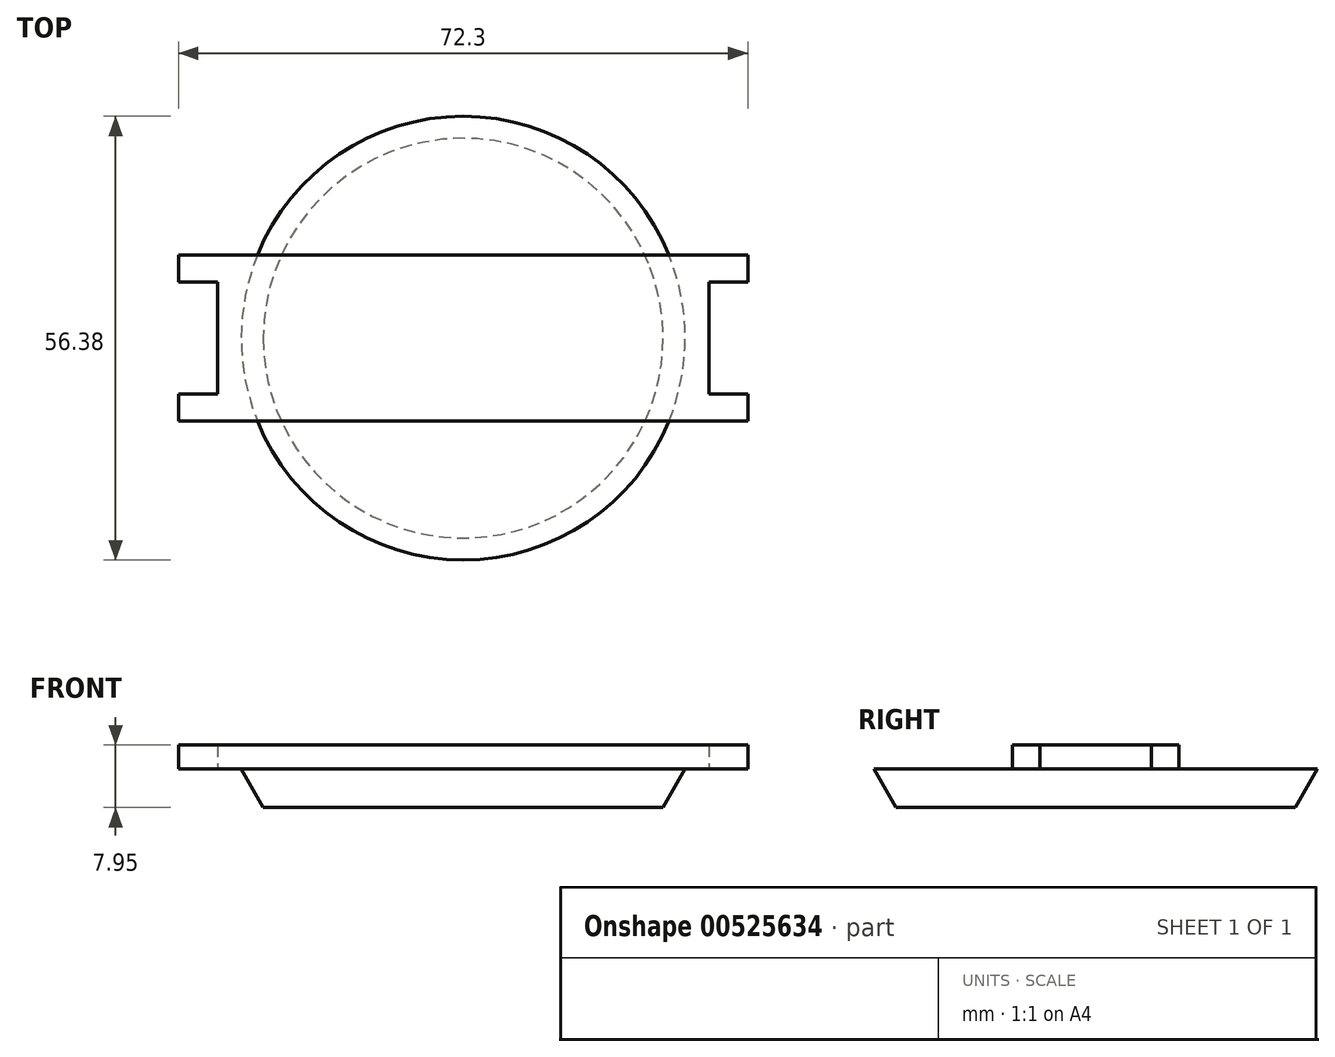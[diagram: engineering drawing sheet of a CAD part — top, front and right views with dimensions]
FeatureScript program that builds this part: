
annotation { "Feature Type Name" : "Feature", "Feature Type Description" : "" }
export const myFeature = defineFeature(function(context is Context, id is Id, definition is map)
    precondition{}
    {
        {
            var Q0;
            Q0=qCreatedBy(makeId("Front.planeOp"),FACE);
            var sketch = newSketch(context, id + "F0", { "sketchPlane" : qUnion([Q0])});
            skLineSegment(sketch, "E0", {"start": v(0, 0) * mm, "end": v(28.19, 0) * mm});
            skLineSegment(sketch, "E1", {"start": v(28.19, 0) * mm, "end": v(25.39, -4.95) * mm});
            skLineSegment(sketch, "E2", {"start": v(25.39, -4.95) * mm, "end": v(0, -4.95) * mm});
            skLineSegment(sketch, "E3", {"start": v(0, -4.95) * mm, "end": v(0, 0) * mm});
            skSolve(sketch);
        }
        {
            var Q0;
            Q0=makeQuery(id+"F0.imprint","IMPRINT",FACE,{"disambiguationData":[TD([[makeQuery(id+"F0.imprint","IMPRINT",EDGE,{"derivedFrom":sQuery(id+"F0.wireOp",EDGE,"E0")}),-1.0]])]});
            var Q1;
            Q1=sQuery(id+"F0.wireOp",EDGE,"E3");
            revolve(context, id + "F1", {"entities" : qUnion([Q0]), "axis" : qUnion([Q1]), "revolveType" : RevolveType.FULL});
        }
        {
            var Q0;
            Q0=qCreatedBy(makeId("Top.planeOp"),FACE);
            var sketch = newSketch(context, id + "F2", { "sketchPlane" : qUnion([Q0])});
            skLineSegment(sketch, "E4", {"start": v(-36.15, -10.54) * mm, "end": v(0, -10.54) * mm});
            skLineSegment(sketch, "E5", {"start": v(-36.15, -10.54) * mm, "end": v(-36.15, -7.1) * mm});
            skLineSegment(sketch, "E6", {"start": v(-36.15, -7.1) * mm, "end": v(-31.2, -7.1) * mm});
            skLineSegment(sketch, "E7", {"start": v(-31.2, -7.1) * mm, "end": v(-31.2, 0) * mm});
            skLineSegment(sketch, "E8.MirrorCS", {"start": v(36.15, -10.54) * mm, "end": v(0, -10.54) * mm});
            skLineSegment(sketch, "E9.MirrorCS", {"start": v(36.15, -7.1) * mm, "end": v(31.2, -7.1) * mm});
            skLineSegment(sketch, "E10.MirrorCS", {"start": v(31.2, -7.1) * mm, "end": v(31.2, 0) * mm});
            skLineSegment(sketch, "E11.MirrorCS", {"start": v(36.15, -10.54) * mm, "end": v(36.15, -7.1) * mm});
            skLineSegment(sketch, "E12.MirrorCS", {"start": v(31.2, 7.1) * mm, "end": v(31.2, 0) * mm});
            skLineSegment(sketch, "E13.MirrorCS", {"start": v(-36.15, 7.1) * mm, "end": v(-31.2, 7.1) * mm});
            skLineSegment(sketch, "E14.MirrorCS", {"start": v(-31.2, 7.1) * mm, "end": v(-31.2, 0) * mm});
            skLineSegment(sketch, "E15.MirrorCS", {"start": v(-36.15, 10.54) * mm, "end": v(0, 10.54) * mm});
            skLineSegment(sketch, "E16.MirrorCS", {"start": v(36.15, 10.54) * mm, "end": v(36.15, 7.1) * mm});
            skLineSegment(sketch, "E17.MirrorCS", {"start": v(-36.15, 10.54) * mm, "end": v(-36.15, 7.1) * mm});
            skLineSegment(sketch, "E18.MirrorCS", {"start": v(36.15, 10.54) * mm, "end": v(0, 10.54) * mm});
            skLineSegment(sketch, "E19.MirrorCS", {"start": v(36.15, 7.1) * mm, "end": v(31.2, 7.1) * mm});
            skSolve(sketch);
        }
        {
            var Q0;
            Q0=makeQuery(id+"F2.imprint","IMPRINT",FACE,{"disambiguationData":[TD([[makeQuery(id+"F2.imprint","IMPRINT",EDGE,{"derivedFrom":sQuery(id+"F2.wireOp",EDGE,"E4")}),1.0]])]});
            extrude(context, id + "F3", {"entities" : qUnion([Q0]), "operationType" : NewBodyOperationType.ADD, "depth" : 3 * mm, "offsetDistance" : 25 * mm});
        }
    });
